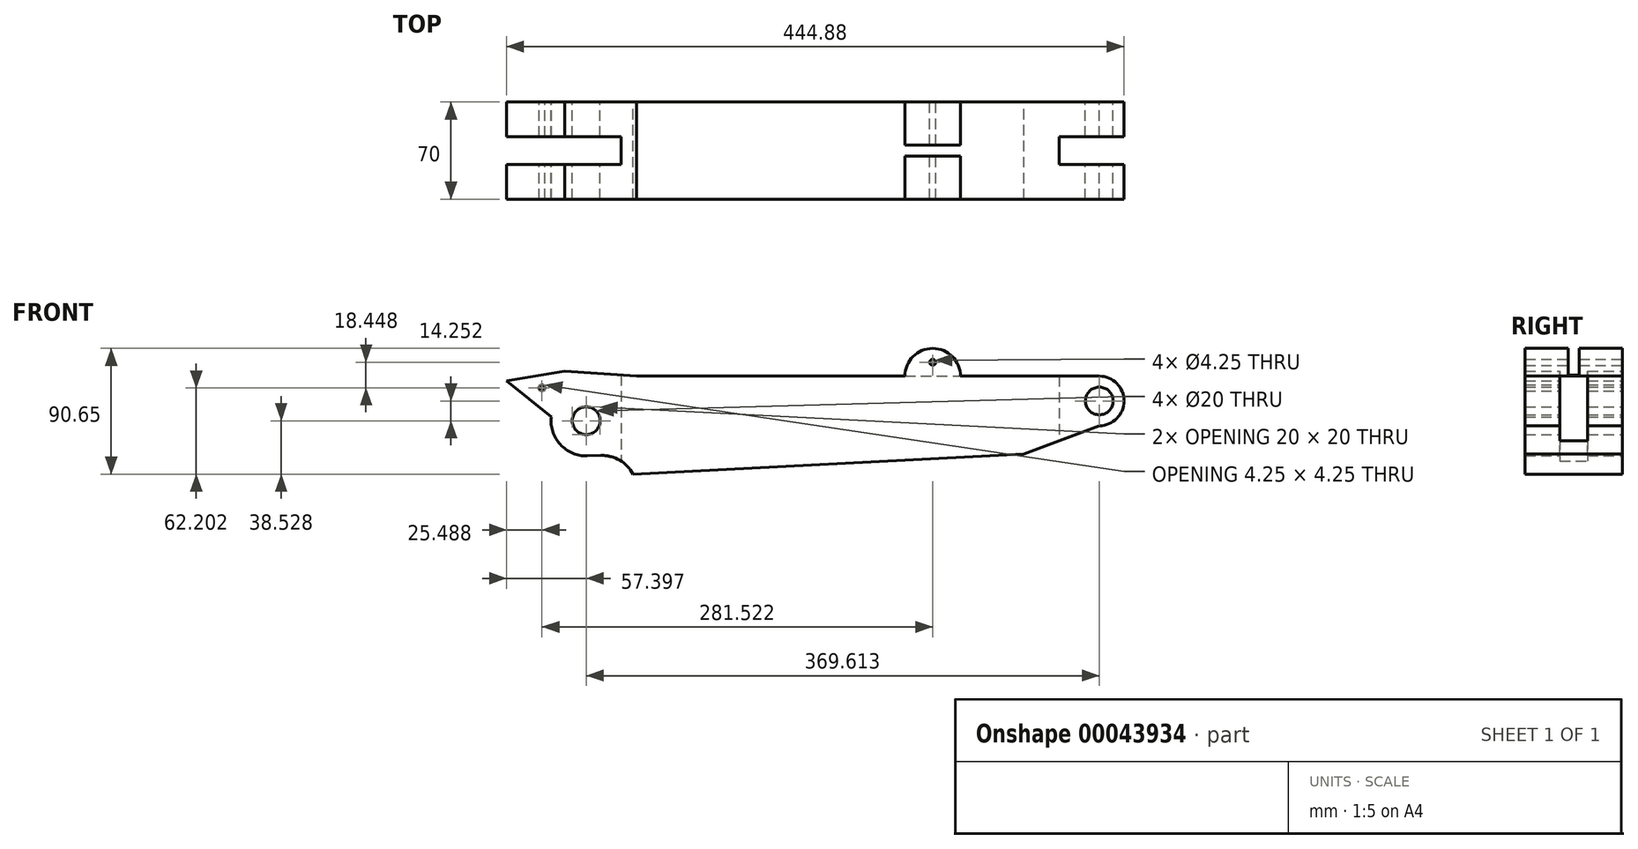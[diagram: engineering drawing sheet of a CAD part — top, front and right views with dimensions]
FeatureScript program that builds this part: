
annotation { "Feature Type Name" : "Feature", "Feature Type Description" : "" }
export const myFeature = defineFeature(function(context is Context, id is Id, definition is map)
    precondition{}
    {
        {
            var Q0;
            Q0=qCreatedBy(makeId("Front.planeOp"),FACE);
            var sketch = newSketch(context, id + "F0", { "sketchPlane" : qUnion([Q0])});
            skLineSegment(sketch, "E0", {"start": v(0, 0) * mm, "end": v(333.3, 0) * mm, "construction": true});
            skSolve(sketch);
        }
        {
            var Q0;
            Q0=qCreatedBy(makeId("Front.planeOp"),FACE);
            var sketch = newSketch(context, id + "F1", { "sketchPlane" : qUnion([Q0])});
            skLineSegment(sketch, "E1", {"start": v(0, 0) * mm, "end": v(333.3, 0) * mm});
            skLineSegment(sketch, "E2", {"start": v(0, 0) * mm, "end": v(-40.71, -7.18) * mm});
            skArc(sketch, "E3", {"start": v(-40.71, -7.18) * mm, "mid": v(-61.51, -34.68) * mm, "end": v(-35.6, -57.44) * mm});
            skLineSegment(sketch, "E4", {"start": v(333.3, 0) * mm, "end": v(333.3, -75.39) * mm, "construction": true});
            skCircle(sketch, "E5", {"center": v(333.3, -17.87) * mm, "radius": 10 * mm});
            skCircle(sketch, "E6", {"center": v(-36.31, -32.12) * mm, "radius": 10 * mm});
            skCircle(sketch, "E7", {"center": v(-68.22, -8.45) * mm, "radius": 2.12 * mm});
            skLineSegment(sketch, "E8", {"start": v(-51.88, 3.46) * mm, "end": v(0, 0) * mm});
            skLineSegment(sketch, "E9", {"start": v(-35.6, -57.44) * mm, "end": v(-25.6, -57.16) * mm});
            skLineSegment(sketch, "E10", {"start": v(278.93, -56.08) * mm, "end": v(-2.56, -70.65) * mm});
            skArc(sketch, "E11", {"start": v(-25.6, -57.16) * mm, "mid": v(-12.15, -60.6) * mm, "end": v(-2.56, -70.65) * mm});
            skLineSegment(sketch, "E12", {"start": v(-61.48, -29.27) * mm, "end": v(-93.7, -3.46) * mm});
            skLineSegment(sketch, "E13", {"start": v(-93.7, -3.46) * mm, "end": v(-51.88, 3.46) * mm});
            skLineSegment(sketch, "E14", {"start": v(278.93, -56.08) * mm, "end": v(333.3, -35.74) * mm});
            skArc(sketch, "E15", {"start": v(333.3, -35.74) * mm, "mid": v(351.17, -17.87) * mm, "end": v(333.3, 0) * mm});
            skSolve(sketch);
        }
        {
            var Q0;
            Q0 = qSketchRegion(id + "F1", true);
            extrude(context, id + "F2", {"entities" : qUnion([Q0]), "depth" : 70 * mm});
        }
        {
            var Q0;
            Q0=qCreatedBy(makeId("Top.planeOp"),FACE);
            var sketch = newSketch(context, id + "F3", { "sketchPlane" : qUnion([Q0])});
            skLineSegment(sketch, "E16.bottom", {"start": v(0, 0) * mm, "end": v(-141.34, 0) * mm, "construction": true});
            skLineSegment(sketch, "E16.top", {"start": v(0, -70) * mm, "end": v(-141.34, -70) * mm, "construction": true});
            skLineSegment(sketch, "E16.left", {"start": v(0, 0) * mm, "end": v(0, -70) * mm, "construction": true});
            skLineSegment(sketch, "E16.right", {"start": v(-141.34, 0) * mm, "end": v(-141.34, -70) * mm, "construction": true});
            skLineSegment(sketch, "E17.bottom", {"start": v(-141.34, -25) * mm, "end": v(-11.08, -25) * mm});
            skLineSegment(sketch, "E17.top", {"start": v(-141.34, -45) * mm, "end": v(-11.08, -45) * mm});
            skLineSegment(sketch, "E17.left", {"start": v(-141.34, -25) * mm, "end": v(-141.34, -45) * mm});
            skLineSegment(sketch, "E17.right", {"start": v(-11.08, -25) * mm, "end": v(-11.08, -45) * mm});
            skLineSegment(sketch, "E18", {"start": v(333.44, 0) * mm, "end": v(333.44, -70) * mm});
            skLineSegment(sketch, "E19.bottom", {"start": v(304.57, -25) * mm, "end": v(358.9, -25) * mm});
            skLineSegment(sketch, "E19.top", {"start": v(304.57, -45) * mm, "end": v(358.9, -45) * mm});
            skLineSegment(sketch, "E19.left", {"start": v(304.57, -25) * mm, "end": v(304.57, -45) * mm});
            skLineSegment(sketch, "E19.right", {"start": v(358.9, -25) * mm, "end": v(358.9, -45) * mm});
            skSolve(sketch);
        }
        {
            var Q0;
            Q0=makeQuery(id+"F3.imprint","IMPRINT",FACE,{"disambiguationData":[TD([[makeQuery(id+"F3.imprint","IMPRINT",EDGE,{"derivedFrom":sQuery(id+"F3.wireOp",EDGE,"E17.bottom")}),-1.0]])]});
            var Q1;
            {var subQ0=sQuery(id+"F3.wireOp",EDGE,"E19.right");Q1=makeQuery(id+"F3.imprint","IMPRINT",FACE,{"disambiguationData":[TD([[makeQuery(id+"F3.imprint","IMPRINT",EDGE,{"derivedFrom":subQ0}),-1.0]])]});}
            var Q2;
            {var subQ3=sQuery(id+"F3.wireOp",EDGE,"E19.left");Q2=makeQuery(id+"F3.imprint","IMPRINT",FACE,{"disambiguationData":[TD([[makeQuery(id+"F3.imprint","IMPRINT",EDGE,{"derivedFrom":subQ3}),1.0]])]});}
            extrude(context, id + "F4", {"entities" : qUnion([Q0, Q1, Q2]), "operationType" : NewBodyOperationType.REMOVE, "depth" : 100 * mm, "hasSecondDirection" : true, "secondDirectionOppositeDirection" : true, "secondDirectionDepth" : 100 * mm});
        }
        {
            var Q0;
            Q0=qCreatedBy(makeId("Front.planeOp"),FACE);
            var sketch = newSketch(context, id + "F5", { "sketchPlane" : qUnion([Q0])});
            skLineSegment(sketch, "E20", {"start": v(333.3, 0) * mm, "end": v(213.3, 0) * mm, "construction": true});
            skArc(sketch, "E21", {"start": v(233.3, 0) * mm, "mid": v(213.3, 20) * mm, "end": v(193.3, 0) * mm});
            skLineSegment(sketch, "E22", {"start": v(213.3, 0) * mm, "end": v(213.3, 10) * mm, "construction": true});
            skCircle(sketch, "E23", {"center": v(213.3, 10) * mm, "radius": 2.12 * mm});
            skLineSegment(sketch, "E24", {"start": v(193.3, 0) * mm, "end": v(213.3, 0) * mm});
            skLineSegment(sketch, "E25", {"start": v(233.3, 0) * mm, "end": v(213.3, 0) * mm});
            skSolve(sketch);
        }
        {
            var Q0;
            Q0 = qSketchRegion(id + "F5", true);
            extrude(context, id + "F6", {"entities" : qUnion([Q0]), "operationType" : NewBodyOperationType.ADD, "depth" : 70 * mm});
        }
        {
            var Q0;
            Q0=qCreatedBy(makeId("Front.planeOp"),FACE);
            cPlane(context, id + "F7", {"entities" : qUnion([Q0]), "cplaneType" : CPlaneType.OFFSET, "offset" : 35 * mm, "width" : 150 * mm, "height" : 150 * mm});
        }
        {
            var Q0;
            Q0=qCreatedBy(id+"F7.planeOp",FACE);
            var sketch = newSketch(context, id + "F8", { "sketchPlane" : qUnion([Q0])});
            skArc(sketch, "E26.0", {"start": v(233.3, 0) * mm, "mid": v(213.3, 20) * mm, "end": v(193.3, 0) * mm});
            skLineSegment(sketch, "E27", {"start": v(193.3, 0) * mm, "end": v(233.3, 0) * mm});
            skSolve(sketch);
        }
        {
            var Q0;
            Q0 = qSketchRegion(id + "F8", true);
            extrude(context, id + "F9", {"entities" : qUnion([Q0]), "operationType" : NewBodyOperationType.REMOVE, "endBound" : BoundingType.SYMMETRIC, "oppositeDirection" : true, "depth" : 8 * mm});
        }
    });
